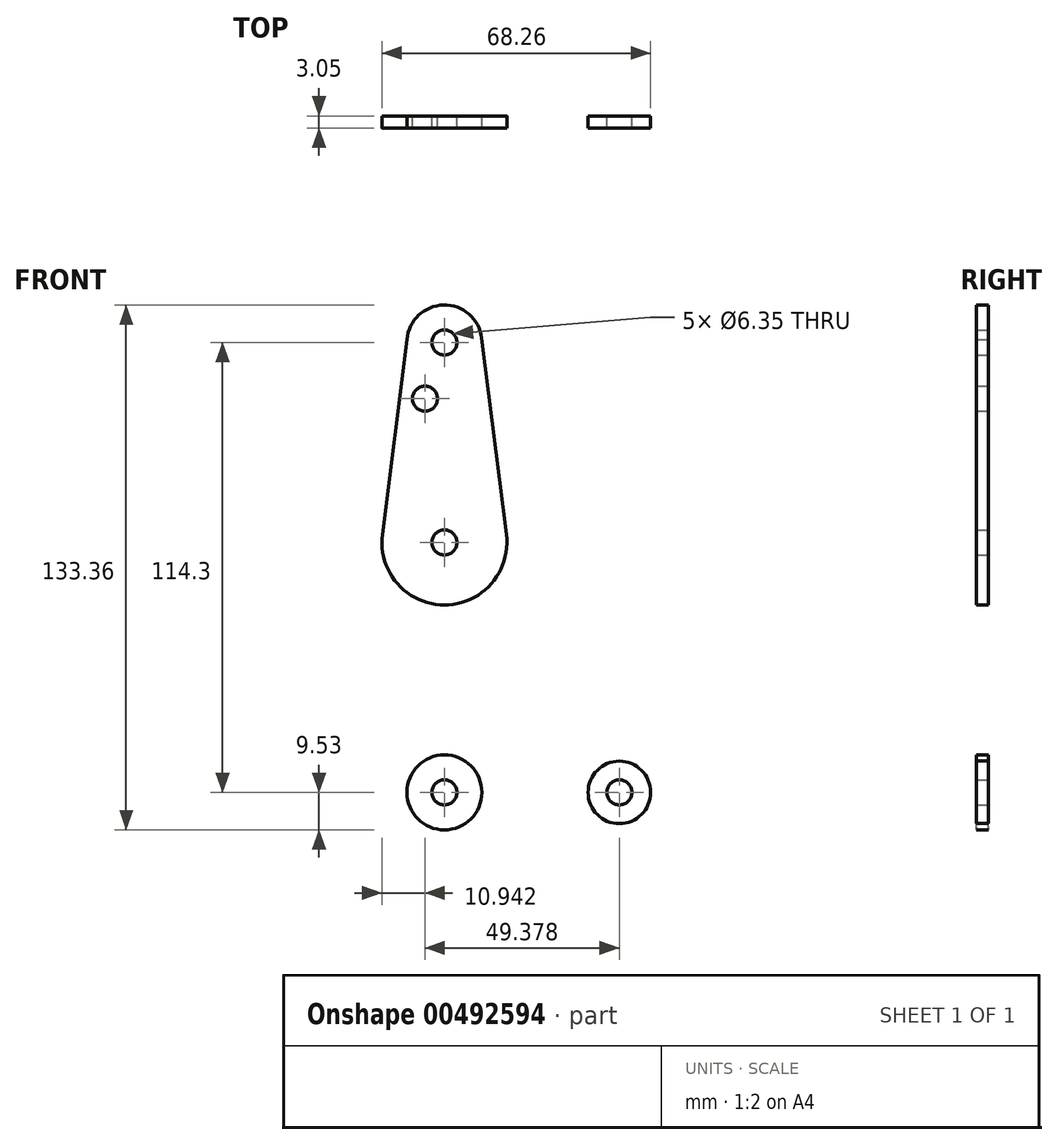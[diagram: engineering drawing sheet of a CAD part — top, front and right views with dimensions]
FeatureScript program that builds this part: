
annotation { "Feature Type Name" : "Feature", "Feature Type Description" : "" }
export const myFeature = defineFeature(function(context is Context, id is Id, definition is map)
    precondition{}
    {
        {
            var Q0;
            Q0=qCreatedBy(makeId("Front.planeOp"),FACE);
            var sketch = newSketch(context, id + "F0", { "sketchPlane" : qUnion([Q0])});
            skLineSegment(sketch, "E0", {"start": v(0, 0) * mm, "end": v(0, 114.3) * mm, "construction": true});
            skLineSegment(sketch, "E1", {"start": v(0, 0) * mm, "end": v(44.45, 0) * mm, "construction": true});
            skCircle(sketch, "E2", {"center": v(0, 114.3) * mm, "radius": 9.53 * mm});
            skCircle(sketch, "E3", {"center": v(0, 63.5) * mm, "radius": 15.88 * mm});
            skCircle(sketch, "E4", {"center": v(0, 0) * mm, "radius": 9.53 * mm});
            skCircle(sketch, "E5", {"center": v(44.45, 0) * mm, "radius": 7.94 * mm});
            skLineSegment(sketch, "E6", {"start": v(9.45, 115.5) * mm, "end": v(15.75, 65.48) * mm});
            skLineSegment(sketch, "E7", {"start": v(-9.5, 115.08) * mm, "end": v(-15.75, 65.49) * mm});
            skLineSegment(sketch, "E8", {"start": v(-15.36, 59.5) * mm, "end": v(-9.48, -0.92) * mm});
            skLineSegment(sketch, "E9", {"start": v(15.7, 61.12) * mm, "end": v(11.33, 17.5) * mm});
            skLineSegment(sketch, "E10", {"start": v(18.98, 8.76) * mm, "end": v(44.7, 7.93) * mm});
            skLineSegment(sketch, "E11", {"start": v(0, -9.53) * mm, "end": v(44.7, -7.93) * mm});
            skCircle(sketch, "E12", {"center": v(-4.93, 100.03) * mm, "radius": 3.18 * mm});
            skCircle(sketch, "E13", {"center": v(0, 0) * mm, "radius": 3.18 * mm});
            skCircle(sketch, "E14", {"center": v(44.45, 0) * mm, "radius": 3.18 * mm});
            skCircle(sketch, "E15", {"center": v(0, 114.3) * mm, "radius": 3.18 * mm});
            skCircle(sketch, "E16", {"center": v(0, 63.5) * mm, "radius": 3.18 * mm});
            skArc(sketch, "E17.filletArc", {"start": v(11.33, 17.5) * mm, "mid": v(13.26, 11.46) * mm, "end": v(18.98, 8.76) * mm});
            skSolve(sketch);
        }
        {
            var Q0;
            Q0 = qSketchRegion(id + "F0", true);
            extrude(context, id + "F1", {"entities" : qUnion([Q0]), "depth" : 3.05 * mm});
        }
    });
